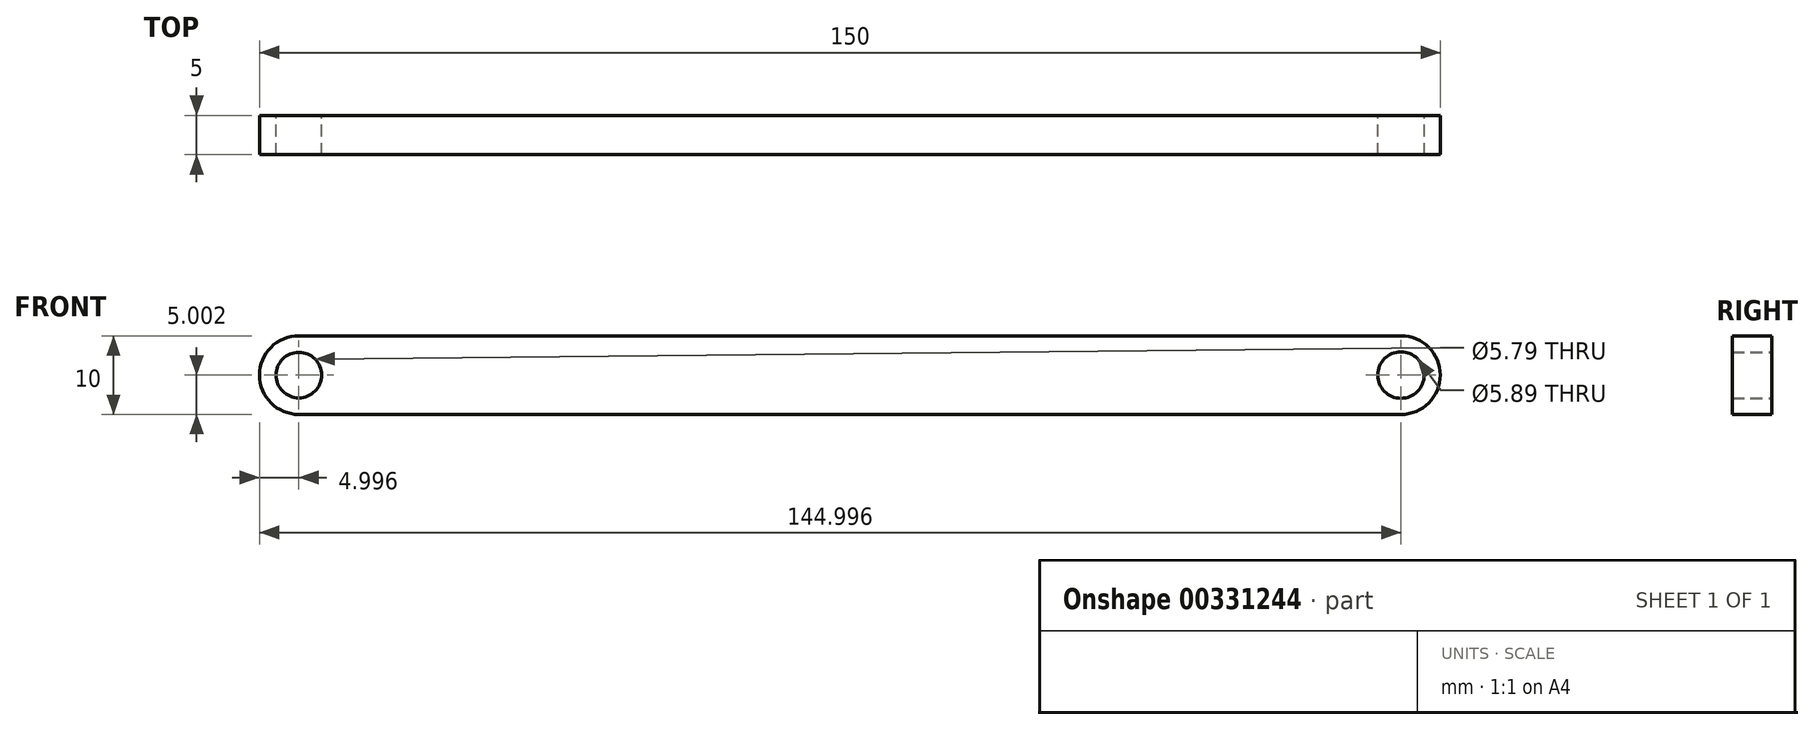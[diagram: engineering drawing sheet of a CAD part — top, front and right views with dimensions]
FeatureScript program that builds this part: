
annotation { "Feature Type Name" : "Feature", "Feature Type Description" : "" }
export const myFeature = defineFeature(function(context is Context, id is Id, definition is map)
    precondition{}
    {
        {
            var Q0;
            Q0=qCreatedBy(makeId("Front.planeOp"),FACE);
            var sketch = newSketch(context, id + "F0", { "sketchPlane" : qUnion([Q0])});
            skLineSegment(sketch, "E0.top", {"start": v(-66.8, -70.67) * mm, "end": v(73.2, -70.67) * mm});
            skArc(sketch, "E1", {"start": v(-66.8, -60.67) * mm, "mid": v(-71.8, -65.67) * mm, "end": v(-66.8, -70.67) * mm});
            skArc(sketch, "E2", {"start": v(73.2, -70.67) * mm, "mid": v(78.2, -65.67) * mm, "end": v(73.2, -60.67) * mm});
            skCircle(sketch, "E3", {"center": v(-66.8, -65.67) * mm, "radius": 2.9 * mm});
            skCircle(sketch, "E4", {"center": v(73.2, -65.67) * mm, "radius": 2.94 * mm});
            skLineSegment(sketch, "E5", {"start": v(-66.8, -60.67) * mm, "end": v(73.2, -60.67) * mm});
            skSolve(sketch);
        }
        {
            var Q0;
            Q0 = qSketchRegion(id + "F0", true);
            extrude(context, id + "F1", {"entities" : qUnion([Q0]), "depth" : 5 * mm});
        }
        {
            var Q0;
            Q0=qCreatedBy(makeId("Front.planeOp"),FACE);
            var sketch = newSketch(context, id + "F2", { "sketchPlane" : qUnion([Q0])});
            skCircle(sketch, "E6", {"center": v(-51.15, 6.32) * mm, "radius": 6.54 * mm});
            skSolve(sketch);
        }
        {
            var Q0;
            Q0=makeQuery(id+"F2.imprint","IMPRINT",FACE,{"disambiguationData":[TD([[makeQuery(id+"F2.imprint","IMPRINT",EDGE,{"derivedFrom":sQuery(id+"F2.wireOp",EDGE,"E6")}),1.0]])]});
            extrude(context, id + "F3", {"entities" : qUnion([Q0]), "depth" : 150 * mm});
        }
        {
            var Q0;
            Q0=makeQuery(id+"F3.opExtrude","SWEPT_BODY",BODY,{"disambiguationData":[OSD([sQuery(id+"F2.wireOp",EDGE,"E6")])]});
            deleteBodies(context, id + "F4", {"entities" : qUnion([Q0])});
        }
    });
